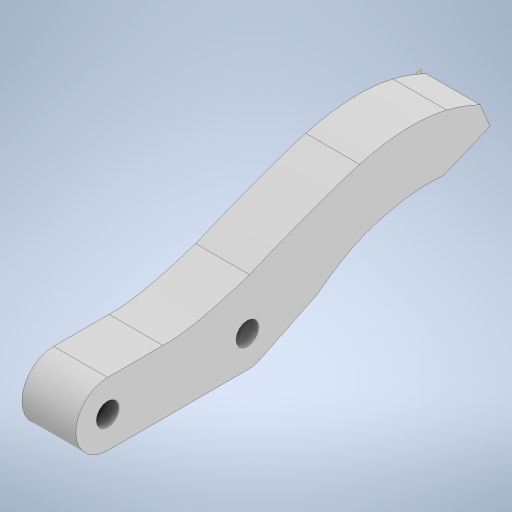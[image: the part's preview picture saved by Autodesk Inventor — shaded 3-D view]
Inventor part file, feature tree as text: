
AUTODESK INVENTOR PART (.ipt)
format: ipt  version: 2024.1 (Build 281209000, 209)  size: 259,584 bytes
history: native  units: in
note: dims shown in document units (in); Inventor stores cm internally (conversion verified against a paired STEP export)
features: plane x1, extrude x1, fillet x1, sketch x1
ambient origin geometry x8: Origin, YZ Plane, XZ Plane, XY Plane, X Axis, Y Axis, Z Axis, Center Point
bodies: Solid1 (feature_tree)
feature tree (4):
  plane  "Work Plane1"
  extrude  "Extrusion1"  Depth=4.9987in
  fillet  "Fillet1"  Radius=8.5in
  sketch  "Sketch1"  dims[d0=3.5433in d1=3.5433in d2=8.5in d3=0.0in d4=3.937in d5=4.9987in]
